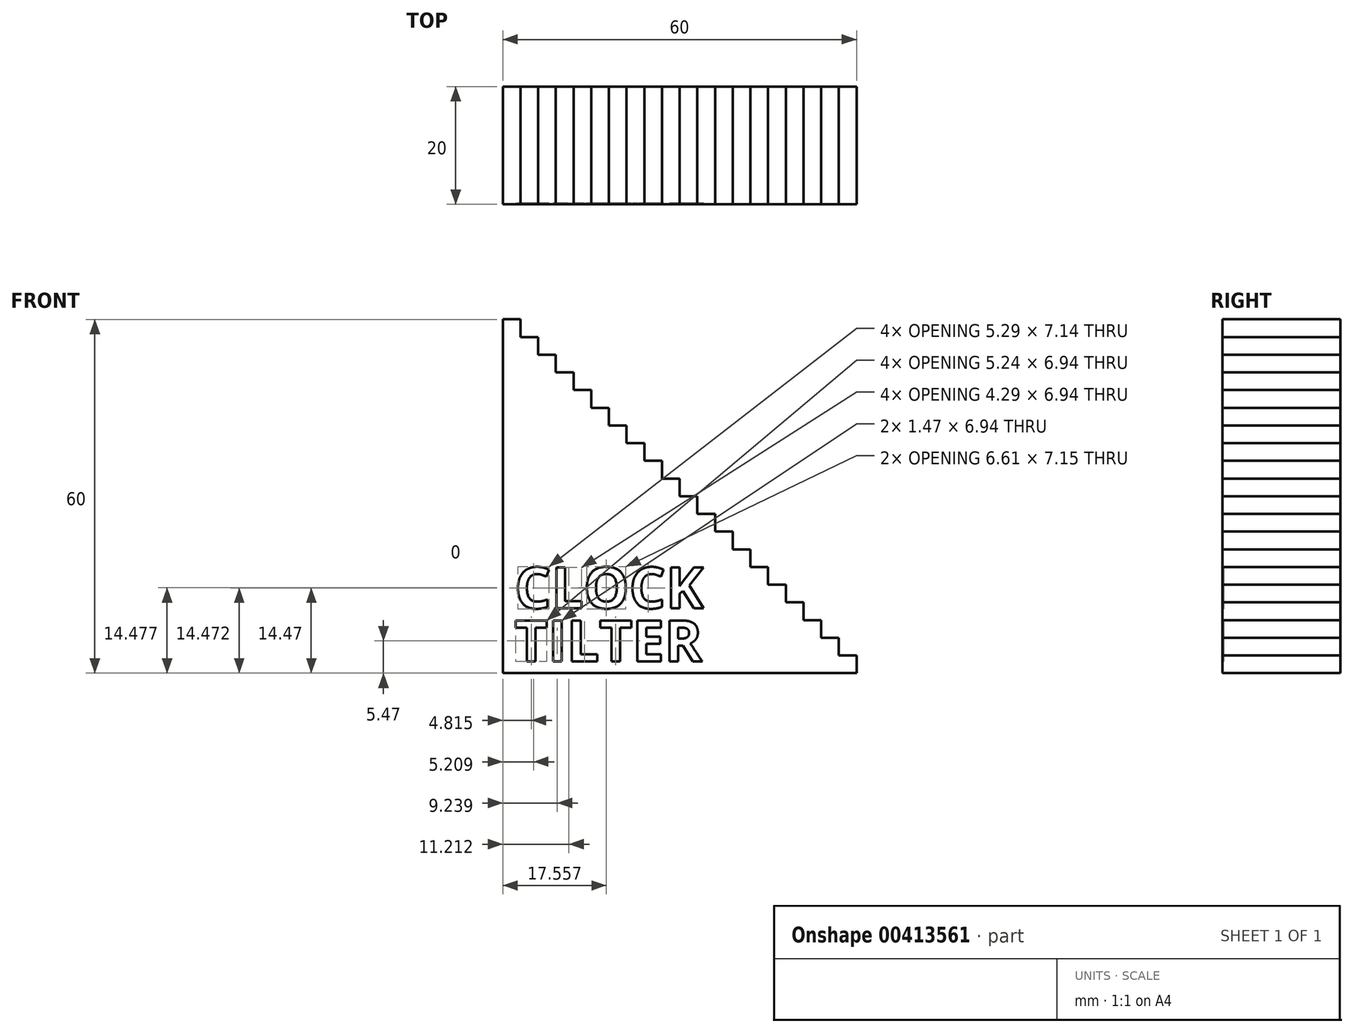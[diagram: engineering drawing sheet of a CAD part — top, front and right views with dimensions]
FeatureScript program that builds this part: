
annotation { "Feature Type Name" : "Feature", "Feature Type Description" : "" }
export const myFeature = defineFeature(function(context is Context, id is Id, definition is map)
    precondition{}
    {
        {
            var Q0;
            Q0=qCreatedBy(makeId("Front.planeOp"),FACE);
            var sketch = newSketch(context, id + "F0", { "sketchPlane" : qUnion([Q0])});
            skLineSegment(sketch, "E0", {"start": v(22.36, -13.42) * mm, "end": v(22.36, -10.42) * mm});
            skLineSegment(sketch, "E1", {"start": v(22.36, -10.42) * mm, "end": v(19.36, -10.42) * mm});
            skLineSegment(sketch, "E2.0.1.0", {"start": v(19.36, -7.42) * mm, "end": v(16.36, -7.42) * mm});
            skLineSegment(sketch, "E2.0.1.1", {"start": v(19.36, -10.42) * mm, "end": v(19.36, -7.42) * mm});
            skLineSegment(sketch, "E2.0.2.0", {"start": v(16.36, -4.42) * mm, "end": v(13.36, -4.42) * mm});
            skLineSegment(sketch, "E2.0.2.1", {"start": v(16.36, -7.42) * mm, "end": v(16.36, -4.42) * mm});
            skLineSegment(sketch, "E2.0.3.0", {"start": v(13.36, -1.42) * mm, "end": v(10.36, -1.42) * mm});
            skLineSegment(sketch, "E2.0.3.1", {"start": v(13.36, -4.42) * mm, "end": v(13.36, -1.42) * mm});
            skLineSegment(sketch, "E2.0.4.0", {"start": v(10.36, 1.58) * mm, "end": v(7.36, 1.58) * mm});
            skLineSegment(sketch, "E2.0.4.1", {"start": v(10.36, -1.42) * mm, "end": v(10.36, 1.58) * mm});
            skLineSegment(sketch, "E2.0.5.0", {"start": v(7.36, 4.58) * mm, "end": v(4.36, 4.58) * mm});
            skLineSegment(sketch, "E2.0.5.1", {"start": v(7.36, 1.58) * mm, "end": v(7.36, 4.58) * mm});
            skLineSegment(sketch, "E2.0.6.0", {"start": v(4.36, 7.58) * mm, "end": v(1.36, 7.58) * mm});
            skLineSegment(sketch, "E2.0.6.1", {"start": v(4.36, 4.58) * mm, "end": v(4.36, 7.58) * mm});
            skLineSegment(sketch, "E2.0.7.0", {"start": v(1.36, 10.58) * mm, "end": v(-1.64, 10.58) * mm});
            skLineSegment(sketch, "E2.0.7.1", {"start": v(1.36, 7.58) * mm, "end": v(1.36, 10.58) * mm});
            skLineSegment(sketch, "E2.0.8.0", {"start": v(-1.64, 13.58) * mm, "end": v(-4.64, 13.58) * mm});
            skLineSegment(sketch, "E2.0.8.1", {"start": v(-1.64, 10.58) * mm, "end": v(-1.64, 13.58) * mm});
            skLineSegment(sketch, "E2.0.9.0", {"start": v(-4.64, 16.58) * mm, "end": v(-7.64, 16.58) * mm});
            skLineSegment(sketch, "E2.0.9.1", {"start": v(-4.64, 13.58) * mm, "end": v(-4.64, 16.58) * mm});
            skLineSegment(sketch, "E2.direction1", {"start": v(14.93, -13.42) * mm, "end": v(22.36, -13.42) * mm, "construction": true});
            skLineSegment(sketch, "E2.direction2", {"start": v(22.36, -13.42) * mm, "end": v(19.36, -10.42) * mm, "construction": true});
            skLineSegment(sketch, "E3.0.0.10", {"start": v(-7.64, 19.58) * mm, "end": v(-10.64, 19.58) * mm});
            skLineSegment(sketch, "E3.3.0.10", {"start": v(-7.64, 16.58) * mm, "end": v(-7.64, 19.58) * mm});
            skLineSegment(sketch, "E3.0.0.11", {"start": v(-10.64, 22.58) * mm, "end": v(-13.64, 22.58) * mm});
            skLineSegment(sketch, "E3.3.0.11", {"start": v(-10.64, 19.58) * mm, "end": v(-10.64, 22.58) * mm});
            skLineSegment(sketch, "E3.0.0.12", {"start": v(-13.64, 25.58) * mm, "end": v(-16.64, 25.58) * mm});
            skLineSegment(sketch, "E3.3.0.12", {"start": v(-13.64, 22.58) * mm, "end": v(-13.64, 25.58) * mm});
            skLineSegment(sketch, "E3.0.0.13", {"start": v(-16.64, 28.58) * mm, "end": v(-19.64, 28.58) * mm});
            skLineSegment(sketch, "E3.3.0.13", {"start": v(-16.64, 25.58) * mm, "end": v(-16.64, 28.58) * mm});
            skLineSegment(sketch, "E3.0.0.14", {"start": v(-19.64, 31.58) * mm, "end": v(-22.64, 31.58) * mm});
            skLineSegment(sketch, "E3.3.0.14", {"start": v(-19.64, 28.58) * mm, "end": v(-19.64, 31.58) * mm});
            skLineSegment(sketch, "E3.0.0.15", {"start": v(-22.64, 34.58) * mm, "end": v(-25.64, 34.58) * mm});
            skLineSegment(sketch, "E3.3.0.15", {"start": v(-22.64, 31.58) * mm, "end": v(-22.64, 34.58) * mm});
            skLineSegment(sketch, "E3.0.0.16", {"start": v(-25.64, 37.58) * mm, "end": v(-28.64, 37.58) * mm});
            skLineSegment(sketch, "E3.3.0.16", {"start": v(-25.64, 34.58) * mm, "end": v(-25.64, 37.58) * mm});
            skLineSegment(sketch, "E3.0.0.17", {"start": v(-28.64, 40.58) * mm, "end": v(-31.64, 40.58) * mm});
            skLineSegment(sketch, "E3.3.0.17", {"start": v(-28.64, 37.58) * mm, "end": v(-28.64, 40.58) * mm});
            skLineSegment(sketch, "E3.0.0.18", {"start": v(-31.64, 43.58) * mm, "end": v(-34.64, 43.58) * mm});
            skLineSegment(sketch, "E3.3.0.18", {"start": v(-31.64, 40.58) * mm, "end": v(-31.64, 43.58) * mm});
            skLineSegment(sketch, "E3.0.0.19", {"start": v(-34.64, 46.58) * mm, "end": v(-37.64, 46.58) * mm});
            skLineSegment(sketch, "E3.3.0.19", {"start": v(-34.64, 43.58) * mm, "end": v(-34.64, 46.58) * mm});
            skLineSegment(sketch, "E4", {"start": v(22.36, -13.42) * mm, "end": v(-37.64, -13.42) * mm});
            skPoint(sketch, "E4.endSnap0", {"position": v(18.64, -13.42) * mm});
            skLineSegment(sketch, "E5", {"start": v(-37.64, -13.42) * mm, "end": v(-37.64, 46.58) * mm});
            skText(sketch, "E6", { "text": "CLOCK", "fontName": "OpenSans-Bold.ttf"});
            skText(sketch, "E7", { "text": "TILTER", "fontName": "OpenSans-Bold.ttf"});
            const initialGuessF0  = {"E6": [-0.03564, -0.00242, 1, 0, 0.007], "E7": [-0.03564, -0.01142, 1, 0, 0.007]};
            skSetInitialGuess(sketch, initialGuessF0);
            skSolve(sketch);
        }
        {
            var Q0;
            Q0=makeQuery(id+"F0.imprint","IMPRINT",FACE,{"disambiguationData":[TD([[makeQuery(id+"F0.imprint","IMPRINT",EDGE,{"derivedFrom":sQuery(id+"F0.wireOp",EDGE,"E0")}),1.0]])]});
            var Q1;
            Q1=makeQuery(id+"F0.imprint","IMPRINT",FACE,{"disambiguationData":[TD([[makeQuery(id+"F0.imprint","IMPRINT",EDGE,{"derivedFrom":sQuery(id+"F0.wireOp",EDGE,"E6.sketch_text.stroke-0")}),-1.0]])]});
            var Q2;
            Q2=makeQuery(id+"F0.imprint","IMPRINT",FACE,{"disambiguationData":[TD([[makeQuery(id+"F0.imprint","IMPRINT",EDGE,{"derivedFrom":sQuery(id+"F0.wireOp",EDGE,"E6.sketch_text.stroke-15")}),-1.0]])]});
            var Q3;
            Q3=makeQuery(id+"F0.imprint","IMPRINT",FACE,{"disambiguationData":[TD([[makeQuery(id+"F0.imprint","IMPRINT",EDGE,{"derivedFrom":sQuery(id+"F0.wireOp",EDGE,"E6.sketch_text.stroke-29")}),1.0]])]});
            var Q4;
            Q4=makeQuery(id+"F0.imprint","IMPRINT",FACE,{"disambiguationData":[TD([[makeQuery(id+"F0.imprint","IMPRINT",EDGE,{"derivedFrom":sQuery(id+"F0.wireOp",EDGE,"E6.sketch_text.stroke-35")}),-1.0]])]});
            var Q5;
            Q5=makeQuery(id+"F0.imprint","IMPRINT",FACE,{"disambiguationData":[TD([[makeQuery(id+"F0.imprint","IMPRINT",EDGE,{"derivedFrom":sQuery(id+"F0.wireOp",EDGE,"E6.sketch_text.stroke-50")}),-1.0]])]});
            var Q6;
            Q6=makeQuery(id+"F0.imprint","IMPRINT",FACE,{"disambiguationData":[TD([[makeQuery(id+"F0.imprint","IMPRINT",EDGE,{"derivedFrom":sQuery(id+"F0.wireOp",EDGE,"E7.sketch_text.stroke-0")}),-1.0]])]});
            var Q7;
            Q7=makeQuery(id+"F0.imprint","IMPRINT",FACE,{"disambiguationData":[TD([[makeQuery(id+"F0.imprint","IMPRINT",EDGE,{"derivedFrom":sQuery(id+"F0.wireOp",EDGE,"E7.sketch_text.stroke-8")}),-1.0]])]});
            var Q8;
            Q8=makeQuery(id+"F0.imprint","IMPRINT",FACE,{"disambiguationData":[TD([[makeQuery(id+"F0.imprint","IMPRINT",EDGE,{"derivedFrom":sQuery(id+"F0.wireOp",EDGE,"E7.sketch_text.stroke-12")}),-1.0]])]});
            var Q9;
            Q9=makeQuery(id+"F0.imprint","IMPRINT",FACE,{"disambiguationData":[TD([[makeQuery(id+"F0.imprint","IMPRINT",EDGE,{"derivedFrom":sQuery(id+"F0.wireOp",EDGE,"E7.sketch_text.stroke-18")}),-1.0]])]});
            var Q10;
            Q10=makeQuery(id+"F0.imprint","IMPRINT",FACE,{"disambiguationData":[TD([[makeQuery(id+"F0.imprint","IMPRINT",EDGE,{"derivedFrom":sQuery(id+"F0.wireOp",EDGE,"E7.sketch_text.stroke-26")}),-1.0]])]});
            var Q11;
            Q11=makeQuery(id+"F0.imprint","IMPRINT",FACE,{"disambiguationData":[TD([[makeQuery(id+"F0.imprint","IMPRINT",EDGE,{"derivedFrom":sQuery(id+"F0.wireOp",EDGE,"E7.sketch_text.stroke-38")}),1.0]])]});
            var Q12;
            Q12=makeQuery(id+"F0.imprint","IMPRINT",FACE,{"disambiguationData":[TD([[makeQuery(id+"F0.imprint","IMPRINT",EDGE,{"derivedFrom":sQuery(id+"F0.wireOp",EDGE,"E6.sketch_text.stroke-21")}),-1.0]])]});
            var Q13;
            Q13=makeQuery(id+"F0.imprint","IMPRINT",FACE,{"disambiguationData":[TD([[makeQuery(id+"F0.imprint","IMPRINT",EDGE,{"derivedFrom":sQuery(id+"F0.wireOp",EDGE,"E7.sketch_text.stroke-38")}),-1.0]])]});
            extrude(context, id + "F1", {"entities" : qUnion([Q0, Q1, Q2, Q3, Q4, Q5, Q6, Q7, Q8, Q9, Q10, Q11, Q12, Q13]), "oppositeDirection" : true, "depth" : 20 * mm});
        }
        {
            var Q0;
            Q0=makeQuery(id+"F0.imprint","IMPRINT",FACE,{"disambiguationData":[TD([[makeQuery(id+"F0.imprint","IMPRINT",EDGE,{"derivedFrom":sQuery(id+"F0.wireOp",EDGE,"E6.sketch_text.stroke-0")}),-1.0]])]});
            var Q1;
            Q1=makeQuery(id+"F0.imprint","IMPRINT",FACE,{"disambiguationData":[TD([[makeQuery(id+"F0.imprint","IMPRINT",EDGE,{"derivedFrom":sQuery(id+"F0.wireOp",EDGE,"E6.sketch_text.stroke-15")}),-1.0]])]});
            var Q2;
            Q2=makeQuery(id+"F0.imprint","IMPRINT",FACE,{"disambiguationData":[TD([[makeQuery(id+"F0.imprint","IMPRINT",EDGE,{"derivedFrom":sQuery(id+"F0.wireOp",EDGE,"E6.sketch_text.stroke-21")}),-1.0]])]});
            var Q3;
            Q3=makeQuery(id+"F0.imprint","IMPRINT",FACE,{"disambiguationData":[TD([[makeQuery(id+"F0.imprint","IMPRINT",EDGE,{"derivedFrom":sQuery(id+"F0.wireOp",EDGE,"E6.sketch_text.stroke-35")}),-1.0]])]});
            var Q4;
            Q4=makeQuery(id+"F0.imprint","IMPRINT",FACE,{"disambiguationData":[TD([[makeQuery(id+"F0.imprint","IMPRINT",EDGE,{"derivedFrom":sQuery(id+"F0.wireOp",EDGE,"E6.sketch_text.stroke-50")}),-1.0]])]});
            var Q5;
            Q5=makeQuery(id+"F0.imprint","IMPRINT",FACE,{"disambiguationData":[TD([[makeQuery(id+"F0.imprint","IMPRINT",EDGE,{"derivedFrom":sQuery(id+"F0.wireOp",EDGE,"E7.sketch_text.stroke-38")}),-1.0]])]});
            var Q6;
            Q6=makeQuery(id+"F0.imprint","IMPRINT",FACE,{"disambiguationData":[TD([[makeQuery(id+"F0.imprint","IMPRINT",EDGE,{"derivedFrom":sQuery(id+"F0.wireOp",EDGE,"E7.sketch_text.stroke-26")}),-1.0]])]});
            var Q7;
            Q7=makeQuery(id+"F0.imprint","IMPRINT",FACE,{"disambiguationData":[TD([[makeQuery(id+"F0.imprint","IMPRINT",EDGE,{"derivedFrom":sQuery(id+"F0.wireOp",EDGE,"E7.sketch_text.stroke-18")}),-1.0]])]});
            var Q8;
            Q8=makeQuery(id+"F0.imprint","IMPRINT",FACE,{"disambiguationData":[TD([[makeQuery(id+"F0.imprint","IMPRINT",EDGE,{"derivedFrom":sQuery(id+"F0.wireOp",EDGE,"E7.sketch_text.stroke-12")}),-1.0]])]});
            var Q9;
            Q9=makeQuery(id+"F0.imprint","IMPRINT",FACE,{"disambiguationData":[TD([[makeQuery(id+"F0.imprint","IMPRINT",EDGE,{"derivedFrom":sQuery(id+"F0.wireOp",EDGE,"E7.sketch_text.stroke-8")}),-1.0]])]});
            var Q10;
            Q10=makeQuery(id+"F0.imprint","IMPRINT",FACE,{"disambiguationData":[TD([[makeQuery(id+"F0.imprint","IMPRINT",EDGE,{"derivedFrom":sQuery(id+"F0.wireOp",EDGE,"E7.sketch_text.stroke-0")}),-1.0]])]});
            extrude(context, id + "F2", {"entities" : qUnion([Q0, Q1, Q2, Q3, Q4, Q5, Q6, Q7, Q8, Q9, Q10]), "operationType" : NewBodyOperationType.REMOVE, "oppositeDirection" : true, "depth" : .2 * mm});
        }
    });
